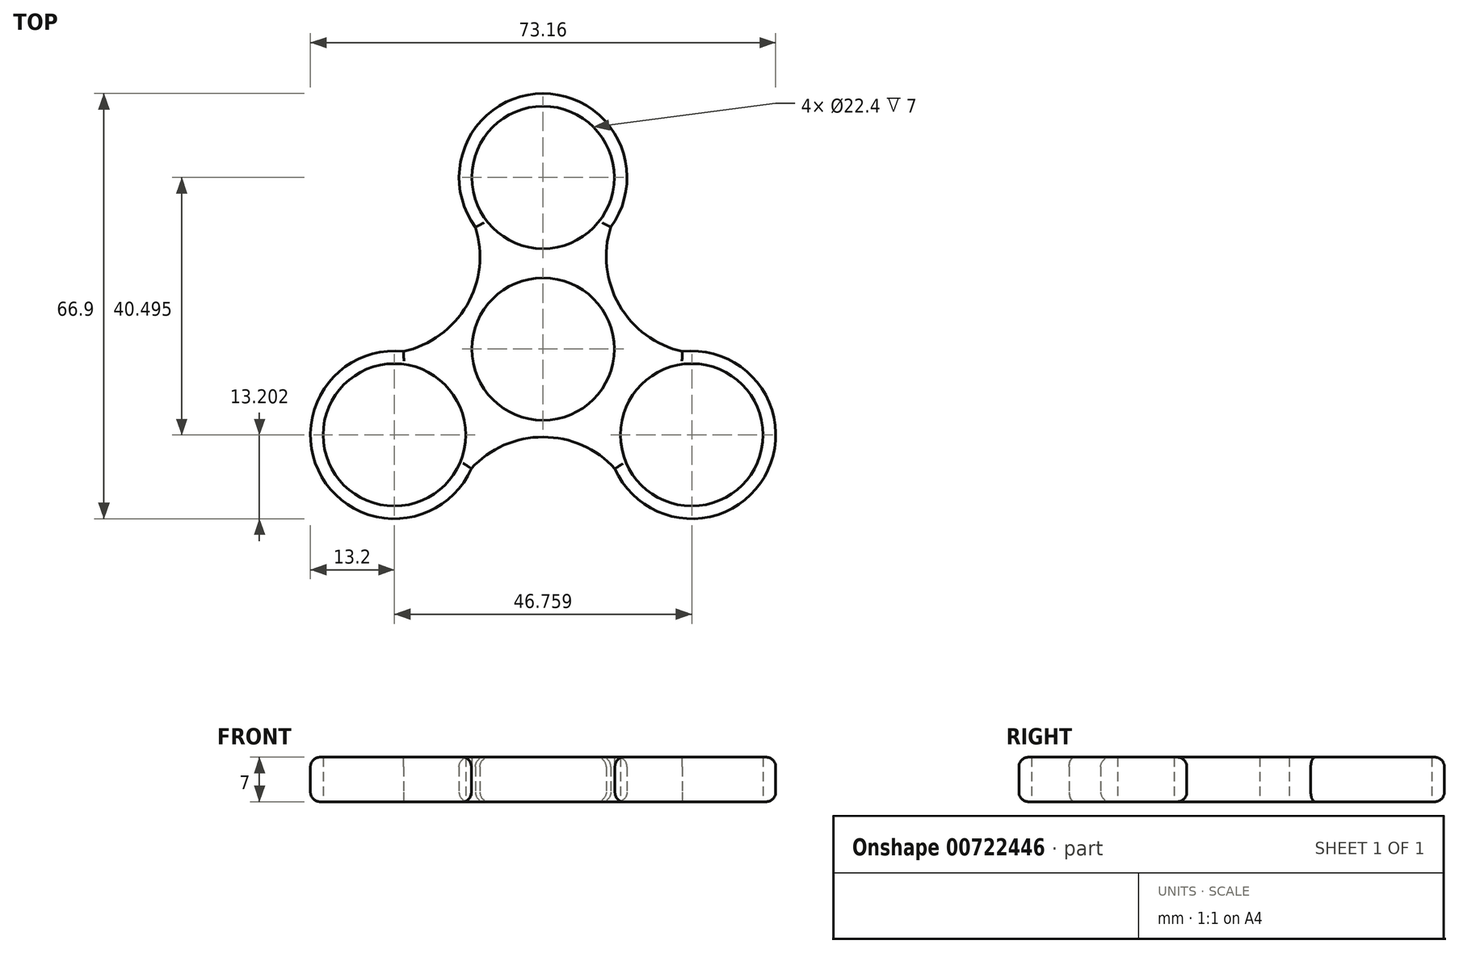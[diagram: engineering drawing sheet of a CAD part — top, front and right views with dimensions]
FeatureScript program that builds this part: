
annotation { "Feature Type Name" : "Feature", "Feature Type Description" : "" }
export const myFeature = defineFeature(function(context is Context, id is Id, definition is map)
    precondition{}
    {
        {
            var Q0;
            Q0=qCreatedBy(makeId("Top.planeOp"),FACE);
            var sketch = newSketch(context, id + "F0", { "sketchPlane" : qUnion([Q0])});
            skCircle(sketch, "E0", {"center": v(0, 0) * mm, "radius": 11.2 * mm});
            skCircle(sketch, "E1", {"center": v(0, 27) * mm, "radius": 11.2 * mm});
            skArc(sketch, "E2", {"start": v(10.65, 19.2) * mm, "mid": v(-0.02, 40.2) * mm, "end": v(-10.63, 19.17) * mm});
            skArc(sketch, "E3.1.0", {"start": v(-21.95, -0.38) * mm, "mid": v(-34.8, -20.11) * mm, "end": v(-11.29, -18.79) * mm});
            skCircle(sketch, "E3.1.1", {"center": v(-23.38, -13.5) * mm, "radius": 11.2 * mm});
            skArc(sketch, "E3.2.0", {"start": v(11.3, -18.82) * mm, "mid": v(34.82, -20.08) * mm, "end": v(21.91, -0.38) * mm});
            skCircle(sketch, "E3.2.1", {"center": v(23.38, -13.5) * mm, "radius": 11.2 * mm});
            skArc(sketch, "E4", {"start": v(10.65, 19.2) * mm, "mid": v(11.97, 6.93) * mm, "end": v(21.91, -0.38) * mm});
            skArc(sketch, "E5.1.0", {"start": v(-21.95, -0.38) * mm, "mid": v(-11.99, 6.9) * mm, "end": v(-10.63, 19.17) * mm});
            skArc(sketch, "E5.2.0", {"start": v(11.3, -18.82) * mm, "mid": v(0.01, -13.83) * mm, "end": v(-11.29, -18.79) * mm});
            skSolve(sketch);
        }
        {
            var Q0;
            Q0=makeQuery(id+"F0.imprint","IMPRINT",FACE,{"disambiguationData":[TD([[makeQuery(id+"F0.imprint","IMPRINT",EDGE,{"derivedFrom":sQuery(id+"F0.wireOp",EDGE,"E0")}),-1.0]])]});
            extrude(context, id + "F1", {"entities" : qUnion([Q0]), "depth" : 7 * mm, "offsetDistance" : 25 * mm});
        }
        {
            var Q0;
            Q0=makeQuery(id+"F1.opExtrude","CAP_EDGE",EDGE,{"disambiguationData":[OSD([sQuery(id+"F0.wireOp",EDGE,"E5.2.0")])],"isStart":false});
            var Q1;
            Q1=makeQuery(id+"F1.opExtrude","CAP_EDGE",EDGE,{"disambiguationData":[OSD([sQuery(id+"F0.wireOp",EDGE,"E3.1.0")])],"isStart":false});
            var Q2;
            Q2=makeQuery(id+"F1.opExtrude","CAP_EDGE",EDGE,{"disambiguationData":[OSD([sQuery(id+"F0.wireOp",EDGE,"E5.1.0")])],"isStart":false});
            var Q3;
            Q3=makeQuery(id+"F1.opExtrude","CAP_EDGE",EDGE,{"disambiguationData":[OSD([sQuery(id+"F0.wireOp",EDGE,"E2")])],"isStart":false});
            var Q4;
            Q4=makeQuery(id+"F1.opExtrude","CAP_EDGE",EDGE,{"disambiguationData":[OSD([sQuery(id+"F0.wireOp",EDGE,"E4")])],"isStart":false});
            var Q5;
            Q5=makeQuery(id+"F1.opExtrude","CAP_EDGE",EDGE,{"disambiguationData":[OSD([sQuery(id+"F0.wireOp",EDGE,"E3.2.0")])],"isStart":false});
            fillet(context, id + "F2", {"entities" : qUnion([Q0, Q1, Q2, Q3, Q4, Q5]), "radius" : 1.5 * mm, "tangentPropagation" : true, "allowEdgeOverflow" : false});
        }
        {
            var Q0;
            Q0=makeQuery(id+"F1.opExtrude","CAP_EDGE",EDGE,{"disambiguationData":[OSD([sQuery(id+"F0.wireOp",EDGE,"E5.1.0")])],"isStart":true});
            var Q1;
            Q1=makeQuery(id+"F1.opExtrude","CAP_EDGE",EDGE,{"disambiguationData":[OSD([sQuery(id+"F0.wireOp",EDGE,"E3.1.0")])],"isStart":true});
            var Q2;
            Q2=makeQuery(id+"F1.opExtrude","CAP_EDGE",EDGE,{"disambiguationData":[OSD([sQuery(id+"F0.wireOp",EDGE,"E5.2.0")])],"isStart":true});
            var Q3;
            Q3=makeQuery(id+"F1.opExtrude","CAP_EDGE",EDGE,{"disambiguationData":[OSD([sQuery(id+"F0.wireOp",EDGE,"E3.2.0")])],"isStart":true});
            var Q4;
            Q4=makeQuery(id+"F1.opExtrude","CAP_EDGE",EDGE,{"disambiguationData":[OSD([sQuery(id+"F0.wireOp",EDGE,"E4")])],"isStart":true});
            var Q5;
            Q5=makeQuery(id+"F1.opExtrude","CAP_EDGE",EDGE,{"disambiguationData":[OSD([sQuery(id+"F0.wireOp",EDGE,"E2")])],"isStart":true});
            fillet(context, id + "F3", {"entities" : qUnion([Q0, Q1, Q2, Q3, Q4, Q5]), "radius" : 1.5 * mm, "tangentPropagation" : true, "allowEdgeOverflow" : false});
        }
    });
